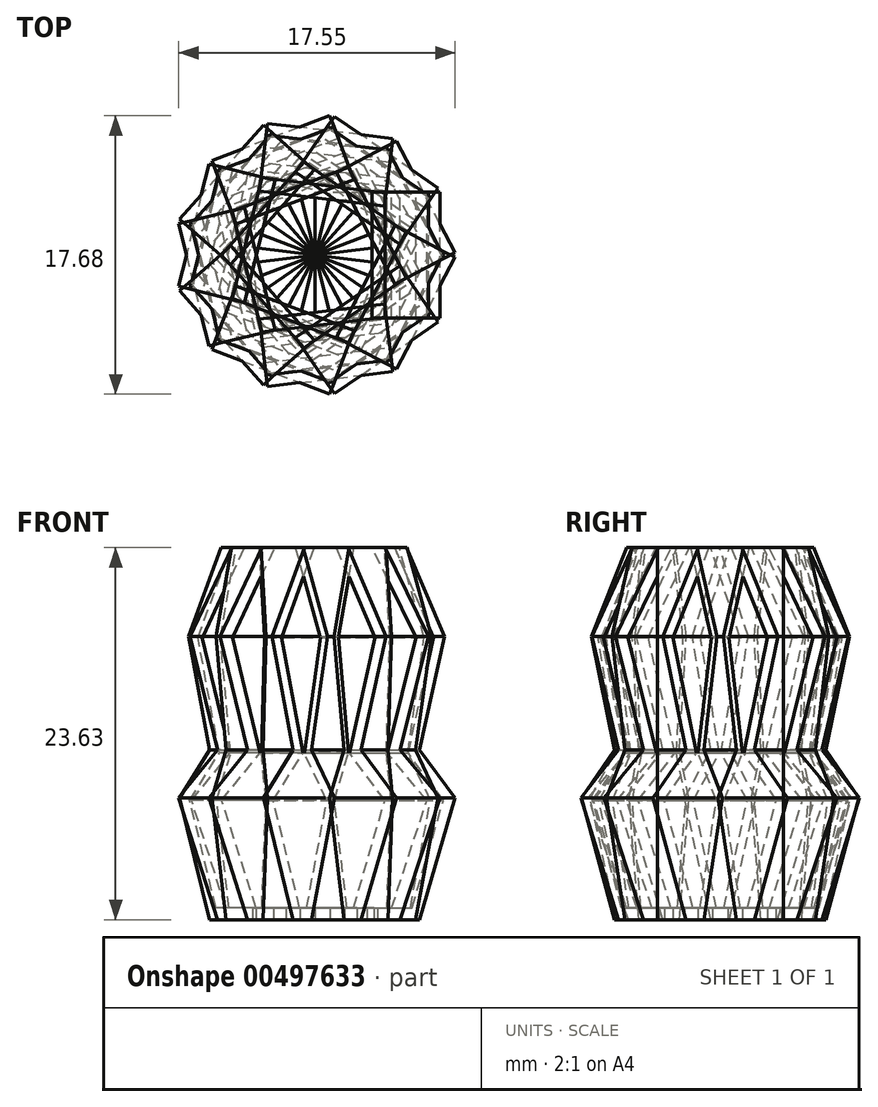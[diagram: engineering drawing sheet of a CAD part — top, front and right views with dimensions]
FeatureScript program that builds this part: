
annotation { "Feature Type Name" : "Feature", "Feature Type Description" : "" }
export const myFeature = defineFeature(function(context is Context, id is Id, definition is map)
    precondition{}
    {
        {
            var Q0;
            Q0=qCreatedBy(makeId("Front.planeOp"),FACE);
            var sketch = newSketch(context, id + "F0", { "sketchPlane" : qUnion([Q0])});
            skLineSegment(sketch, "E0", {"start": v(0, 0) * mm, "end": v(5.4, 0) * mm});
            skLineSegment(sketch, "E1", {"start": v(0, 2.1) * mm, "end": v(0, 0) * mm});
            skLineSegment(sketch, "E2.0", {"start": v(0, 0.75) * mm, "end": v(4.86, 0.75) * mm});
            skLineSegment(sketch, "E3", {"start": v(5.4, 0) * mm, "end": v(7.94, 7.75) * mm});
            skLineSegment(sketch, "E4", {"start": v(7.94, 7.75) * mm, "end": v(5.4, 10.77) * mm});
            skLineSegment(sketch, "E5", {"start": v(5.4, 10.77) * mm, "end": v(7.2, 18) * mm});
            skLineSegment(sketch, "E6", {"start": v(7.2, 18) * mm, "end": v(4.45, 23.63) * mm});
            skLineSegment(sketch, "E7.0", {"start": v(6.4, 17.92) * mm, "end": v(3.62, 23.63) * mm});
            skLineSegment(sketch, "E7.1", {"start": v(4.58, 10.58) * mm, "end": v(6.4, 17.92) * mm});
            skLineSegment(sketch, "E7.2", {"start": v(7.1, 7.58) * mm, "end": v(4.58, 10.58) * mm});
            skLineSegment(sketch, "E7.3", {"start": v(4.86, 0.75) * mm, "end": v(7.1, 7.58) * mm});
            skLineSegment(sketch, "E8", {"start": v(3.62, 23.63) * mm, "end": v(4.45, 23.63) * mm});
            skSolve(sketch);
        }
        {
            var Q0;
            Q0=makeQuery(id+"F0.imprint","IMPRINT",FACE,{"disambiguationData":[TD([[makeQuery(id+"F0.imprint","IMPRINT",EDGE,{"derivedFrom":sQuery(id+"F0.wireOp",EDGE,"E0")}),1.0]])]});
            extrude(context, id + "F1", {"entities" : qUnion([Q0]), "depth" : 4 * mm, "hasSecondDirection" : true, "secondDirectionOppositeDirection" : true, "secondDirectionDepth" : 4 * mm});
        }
        {
            var Q0;
            Q0=makeQuery(id+"F1.opExtrude","SWEPT_BODY",BODY,{"disambiguationData":[OSD([sQuery(id+"F0.wireOp",EDGE,"E0"),sQuery(id+"F0.wireOp",EDGE,"T7crRCSO-nWGS-oMrG-bt7b-a5VfY8CambFn"),sQuery(id+"F0.wireOp",EDGE,"xv8VgBhu-qazy-YgqB-v8JE-5yVdrMK1Qche"),sQuery(id+"F0.wireOp",EDGE,"17f4b7c3-1163-45f6-bf05-4113330963bc.0"),sQuery(id+"F0.wireOp",EDGE,"17f4b7c3-1163-45f6-bf05-4113330963bc.1"),sQuery(id+"F0.wireOp",EDGE,"17f4b7c3-1163-45f6-bf05-4113330963bc.2"),sQuery(id+"F0.wireOp",EDGE,"8E1QmZ2g-YMvP-tSYN-84yT-wLBnS1EG7rmy"),sQuery(id+"F0.wireOp",EDGE,"E1")])]});
            var Q1;
            Q1=sQuery(id+"F0.wireOp",EDGE,"E1");
            circularPattern(context, id + "F2", {"entities" : qUnion([Q0]), "axis" : qUnion([Q1]), "angle" : 360 * degree, "instanceCount" : 13, "equalSpace" : true});
        }
    });
